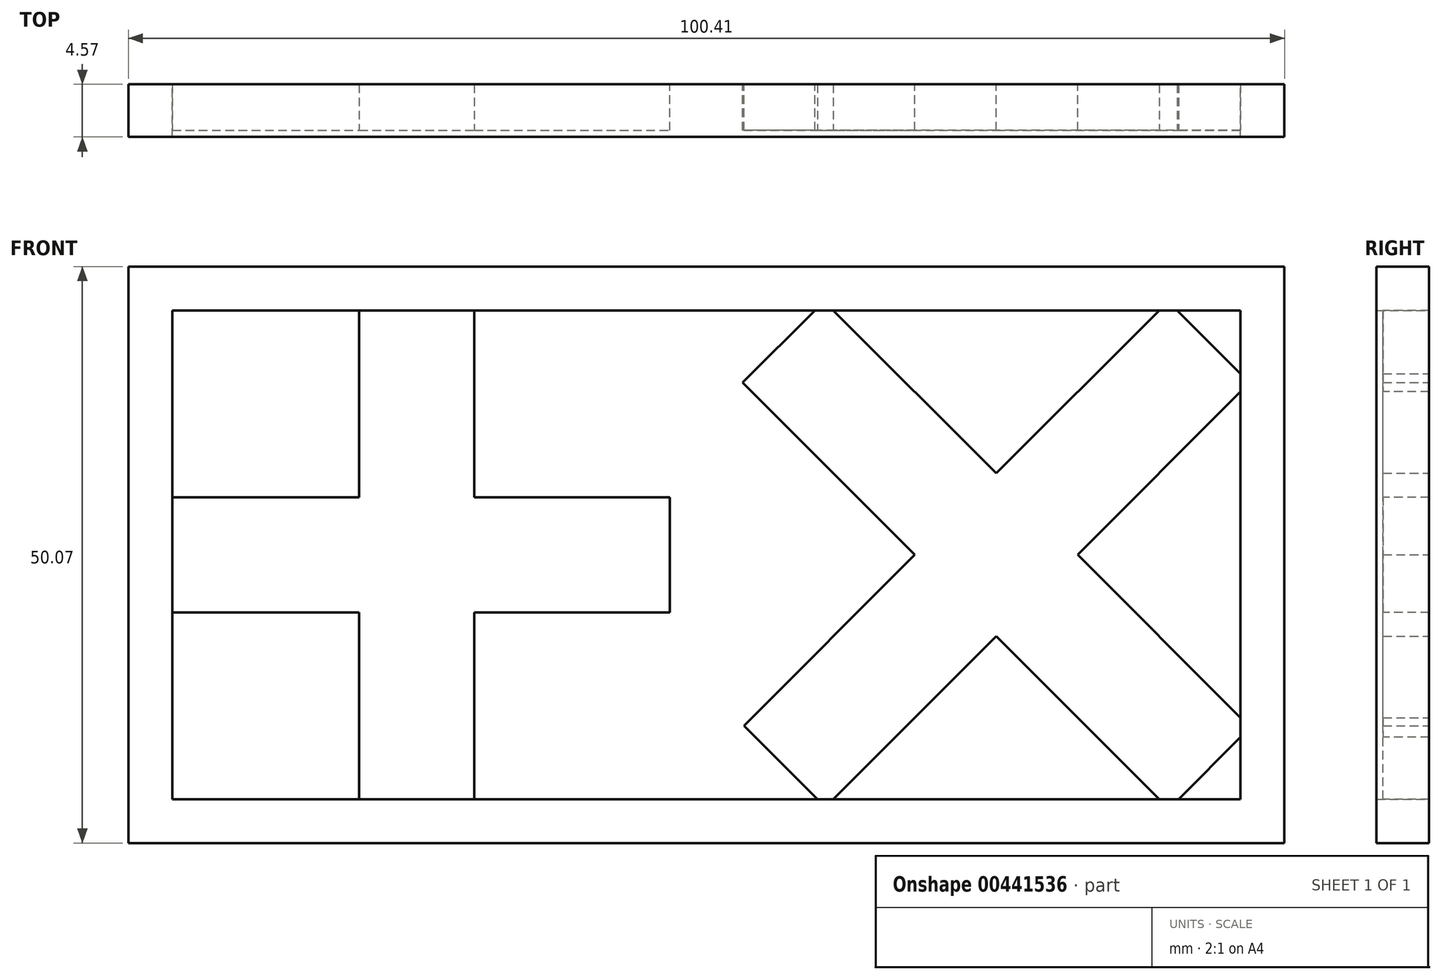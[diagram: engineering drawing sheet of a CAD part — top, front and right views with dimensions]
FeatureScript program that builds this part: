
annotation { "Feature Type Name" : "Feature", "Feature Type Description" : "" }
export const myFeature = defineFeature(function(context is Context, id is Id, definition is map)
    precondition{}
    {
        {
            var Q0;
            Q0=qCreatedBy(makeId("Front.planeOp"),FACE);
            var sketch = newSketch(context, id + "F0", { "sketchPlane" : qUnion([Q0])});
            skLineSegment(sketch, "E0.bottom", {"start": v(-42.85, 23.49) * mm, "end": v(57.56, 23.49) * mm});
            skLineSegment(sketch, "E0.top", {"start": v(-42.85, -26.58) * mm, "end": v(57.56, -26.58) * mm});
            skLineSegment(sketch, "E0.left", {"start": v(-42.85, 23.49) * mm, "end": v(-42.85, -26.58) * mm});
            skLineSegment(sketch, "E0.right", {"start": v(57.56, 23.49) * mm, "end": v(57.56, -26.58) * mm});
            skLineSegment(sketch, "E1.0", {"start": v(53.75, 19.68) * mm, "end": v(53.75, -22.77) * mm});
            skLineSegment(sketch, "E1.1", {"start": v(-39.04, 19.68) * mm, "end": v(53.75, 19.68) * mm});
            skLineSegment(sketch, "E1.2", {"start": v(-39.04, 19.68) * mm, "end": v(-39.04, -22.77) * mm});
            skLineSegment(sketch, "E1.3", {"start": v(-39.04, -22.77) * mm, "end": v(53.75, -22.77) * mm});
            skSolve(sketch);
        }
        {
            var Q0;
            Q0=makeQuery(id+"F0.imprint","IMPRINT",FACE,{"disambiguationData":[TD([[makeQuery(id+"F0.imprint","IMPRINT",EDGE,{"derivedFrom":sQuery(id+"F0.wireOp",EDGE,"E0.bottom")}),-1.0]])]});
            extrude(context, id + "F1", {"entities" : qUnion([Q0]), "depth" : 4.57 * mm});
        }
        {
            var Q0;
            Q0=qCreatedBy(makeId("Front.planeOp"),FACE);
            var sketch = newSketch(context, id + "F2", { "sketchPlane" : qUnion([Q0])});
            skPoint(sketch, "E2", {"position": v(32.52, -1.55) * mm});
            skLineSegment(sketch, "E3.0", {"start": v(54.59, -16.55) * mm, "end": v(39.6, -1.55) * mm});
            skLineSegment(sketch, "E4.0", {"start": v(47.52, -23.62) * mm, "end": v(32.52, -8.62) * mm});
            skLineSegment(sketch, "E5.0", {"start": v(17.68, -23.46) * mm, "end": v(32.52, -8.62) * mm});
            skLineSegment(sketch, "E6.0", {"start": v(10.6, -16.39) * mm, "end": v(25.45, -1.55) * mm});
            skLineSegment(sketch, "E7", {"start": v(47.52, -23.62) * mm, "end": v(54.59, -16.55) * mm});
            skLineSegment(sketch, "E8", {"start": v(17.57, 20.47) * mm, "end": v(10.5, 13.4) * mm});
            skLineSegment(sketch, "E9", {"start": v(54.53, 13.4) * mm, "end": v(47.46, 20.46) * mm});
            skLineSegment(sketch, "E10", {"start": v(17.68, -23.46) * mm, "end": v(10.6, -16.39) * mm});
            skLineSegment(sketch, "E11.trimOffspring", {"start": v(32.52, 5.52) * mm, "end": v(47.46, 20.46) * mm});
            skLineSegment(sketch, "E12.trimOffspring", {"start": v(32.52, 5.52) * mm, "end": v(17.57, 20.47) * mm});
            skLineSegment(sketch, "E13.trimOffspring", {"start": v(39.6, -1.55) * mm, "end": v(54.53, 13.4) * mm});
            skLineSegment(sketch, "E14.trimOffspring", {"start": v(25.45, -1.55) * mm, "end": v(10.5, 13.4) * mm});
            skSolve(sketch);
        }
        {
            var Q0;
            Q0=makeQuery(id+"F2.imprint","IMPRINT",FACE,{"disambiguationData":[TD([[makeQuery(id+"F2.imprint","IMPRINT",EDGE,{"derivedFrom":sQuery(id+"F2.wireOp",EDGE,"E3.0")}),1.0]])]});
            extrude(context, id + "F3", {"entities" : qUnion([Q0]), "operationType" : NewBodyOperationType.ADD, "depth" : 4 * mm});
        }
        {
            var Q0;
            Q0=qCreatedBy(makeId("Front.planeOp"),FACE);
            var sketch = newSketch(context, id + "F4", { "sketchPlane" : qUnion([Q0])});
            skPoint(sketch, "E15", {"position": v(-17.82, -1.55) * mm});
            skLineSegment(sketch, "E16.bottom", {"start": v(-39.82, -6.55) * mm, "end": v(-22.82, -6.55) * mm});
            skLineSegment(sketch, "E16.top", {"start": v(-39.82, 3.45) * mm, "end": v(-22.82, 3.45) * mm});
            skLineSegment(sketch, "E16.left", {"start": v(-39.82, -6.55) * mm, "end": v(-39.82, 3.45) * mm});
            skLineSegment(sketch, "E16.right", {"start": v(4.18, -6.55) * mm, "end": v(4.18, 3.45) * mm});
            skLineSegment(sketch, "E17.bottom", {"start": v(-22.82, -23.55) * mm, "end": v(-12.82, -23.55) * mm});
            skLineSegment(sketch, "E17.top", {"start": v(-22.82, 20.45) * mm, "end": v(-12.82, 20.45) * mm});
            skLineSegment(sketch, "E17.left", {"start": v(-22.82, -23.55) * mm, "end": v(-22.82, -6.55) * mm});
            skLineSegment(sketch, "E17.right", {"start": v(-12.82, -23.55) * mm, "end": v(-12.82, -6.55) * mm});
            skLineSegment(sketch, "E18.trimOffspring", {"start": v(-22.82, 3.45) * mm, "end": v(-22.82, 20.45) * mm});
            skLineSegment(sketch, "E19.trimOffspring", {"start": v(-12.82, -6.55) * mm, "end": v(4.18, -6.55) * mm});
            skLineSegment(sketch, "E20.trimOffspring", {"start": v(-12.82, 3.45) * mm, "end": v(-12.82, 20.45) * mm});
            skLineSegment(sketch, "E21.trimOffspring", {"start": v(-12.82, 3.45) * mm, "end": v(4.18, 3.45) * mm});
            skSolve(sketch);
        }
        {
            var Q0;
            Q0=makeQuery(id+"F4.imprint","IMPRINT",FACE,{"disambiguationData":[TD([[makeQuery(id+"F4.imprint","IMPRINT",EDGE,{"derivedFrom":sQuery(id+"F4.wireOp",EDGE,"E16.bottom")}),1.0]])]});
            extrude(context, id + "F5", {"entities" : qUnion([Q0]), "operationType" : NewBodyOperationType.ADD, "depth" : 4 * mm});
        }
    });
